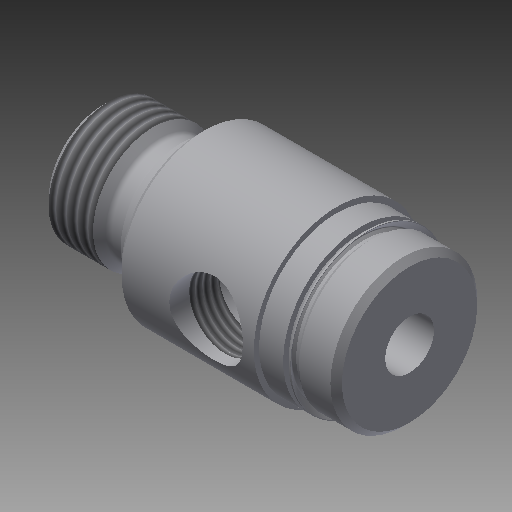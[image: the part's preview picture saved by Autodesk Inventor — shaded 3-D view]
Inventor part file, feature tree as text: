
AUTODESK INVENTOR PART (.ipt)
format: ipt  version: 2019 (Build 230136000, 136)  size: 325,632 bytes
history: native  units: in
note: dims shown in document units (in); Inventor stores cm internally (conversion verified against a paired STEP export)
features: other x119, sketch x6, revolve x5, thread x2, hole x1
ambient origin geometry x8: Origin, YZ Plane, XZ Plane, XY Plane, X Axis, Y Axis, Z Axis, Center Point
bodies: Solid1 (feature_tree)
feature tree (133):
  revolve  "Revolution1"  [1 undecoded]
  thread  "Thread1"  [1 undecoded]
  revolve  "Revolution2"  Angle=360.0deg
  hole  "Hole1"  [1 undecoded]
  revolve  "Revolution3"  [1 undecoded]
  revolve  "Revolution4"  [1 undecoded]
  thread  "Thread2"  [1 undecoded]
  revolve  "Revolution5"  [1 undecoded]
  other  "dp1_XY"
  other  "dp1_YZ"
  other  "dp1_ZX"
  other  "dp1_X"
  other  "dp1_Y"
  other  "dp1_Z"
  other  "dp1_Center"
  other  "dp2_XY"
  other  "dp2_YZ"
  other  "dp2_ZX"
  other  "dp2_X"
  other  "dp2_Y"
  other  "dp2_Z"
  other  "dp2_Center"
  other  "hh_XY"
  other  "hh_YZ"
  other  "hh_ZX"
  other  "hh_X"
  other  "hh_Y"
  other  "hh_Z"
  other  "hh_Center"
  other  "port_XY"
  other  "port_YZ"
  other  "port_ZX"
  other  "port_X"
  other  "port_Y"
  other  "port_Z"
  other  "port_Center"
  other  "rod_guide_XY"
  other  "rod_guide_YZ"
  other  "rod_guide_ZX"
  other  "rod_guide_X"
  other  "rod_guide_Y"
  other  "rod_guide_Z"
  other  "rod_guide_Center"
  other  "s1_XY"
  other  "s1_YZ"
  other  "s1_ZX"
  other  "s1_X"
  other  "s1_Y"
  other  "s1_Z"
  other  "s1_Center"
  other  "s2_XY"
  other  "s2_YZ"
  other  "s2_ZX"
  other  "s2_X"
  other  "s2_Y"
  other  "s2_Z"
  other  "s2_Center"
  other  "t1_XY"
  other  "t1_YZ"
  other  "t1_ZX"
  other  "t1_X"
  other  "t1_Y"
  other  "t1_Z"
  other  "t1_Center"
  other  "t111_XY"
  other  "t111_YZ"
  other  "t111_ZX"
  other  "t111_X"
  other  "t111_Y"
  other  "t111_Z"
  other  "t111_Center"
  other  "to_foot_bracket_XY"
  other  "to_foot_bracket_YZ"
  other  "to_foot_bracket_ZX"
  other  "to_foot_bracket_X"
  other  "to_foot_bracket_Y"
  other  "to_foot_bracket_Z"
  other  "to_foot_bracket_Center"
  other  "to_nut_XY"
  other  "to_nut_YZ"
  other  "to_nut_ZX"
  other  "to_nut_X"
  other  "to_nut_Y"
  other  "to_nut_Z"
  other  "to_nut_Center"
  other  "to_rod_XY"
  other  "to_rod_YZ"
  other  "to_rod_ZX"
  other  "to_rod_X"
  other  "to_rod_Y"
  other  "to_rod_Z"
  other  "to_rod_Center"
  other  "to_screw_XY"
  other  "to_screw_YZ"
  other  "to_screw_ZX"
  other  "to_screw_X"
  other  "to_screw_Y"
  other  "to_screw_Z"
  other  "to_screw_Center"
  other  "to_trunnion_brackets_XY"
  other  "to_trunnion_brackets_YZ"
  other  "to_trunnion_brackets_ZX"
  other  "to_trunnion_brackets_X"
  other  "to_trunnion_brackets_Y"
  other  "to_trunnion_brackets_Z"
  other  "to_trunnion_brackets_Center"
  other  "to_trunnion_brackets1_XY"
  other  "to_trunnion_brackets1_YZ"
  other  "to_trunnion_brackets1_ZX"
  other  "to_trunnion_brackets1_X"
  other  "to_trunnion_brackets1_Y"
  other  "to_trunnion_brackets1_Z"
  other  "to_trunnion_brackets1_Center"
  other  "to_trunnion_brackets2_XY"
  other  "to_trunnion_brackets2_YZ"
  other  "to_trunnion_brackets2_ZX"
  other  "to_trunnion_brackets2_X"
  other  "to_trunnion_brackets2_Y"
  other  "to_trunnion_brackets2_Z"
  other  "to_trunnion_brackets2_Center"
  other  "to_tube_XY"
  other  "to_tube_YZ"
  other  "to_tube_ZX"
  other  "to_tube_X"
  other  "to_tube_Y"
  other  "to_tube_Z"
  other  "to_tube_Center"
  sketch  "Sketch_2"  dims[d0=360.0deg d1=0.23in d2=0.0in d3=360.0deg]
  sketch  "Sketch_3"  dims[d4=0.2535in d5=0.75in d6=0.2735in d7=0.25in d8=90.0deg d9=1.594in d10=0.0in d11=360.0deg]
  sketch  "Sketch3"  dims[d12=360.0deg d13=0.1501in d14=0.0in]
  sketch  "Sketch_10"  dims[d15=360.0deg]
  sketch  "Sketch_40"  dims[d16=0.0in d17=0.0in d18=0.0in d19=0.0in d20=0.0in d21=0.0in]
  sketch  "Sketch_47"
note: 7 required parameter values undecoded (feature->parameter linkage not recoverable at this tier; creation-order binding heuristic only, values carry confidence <= 0.55)